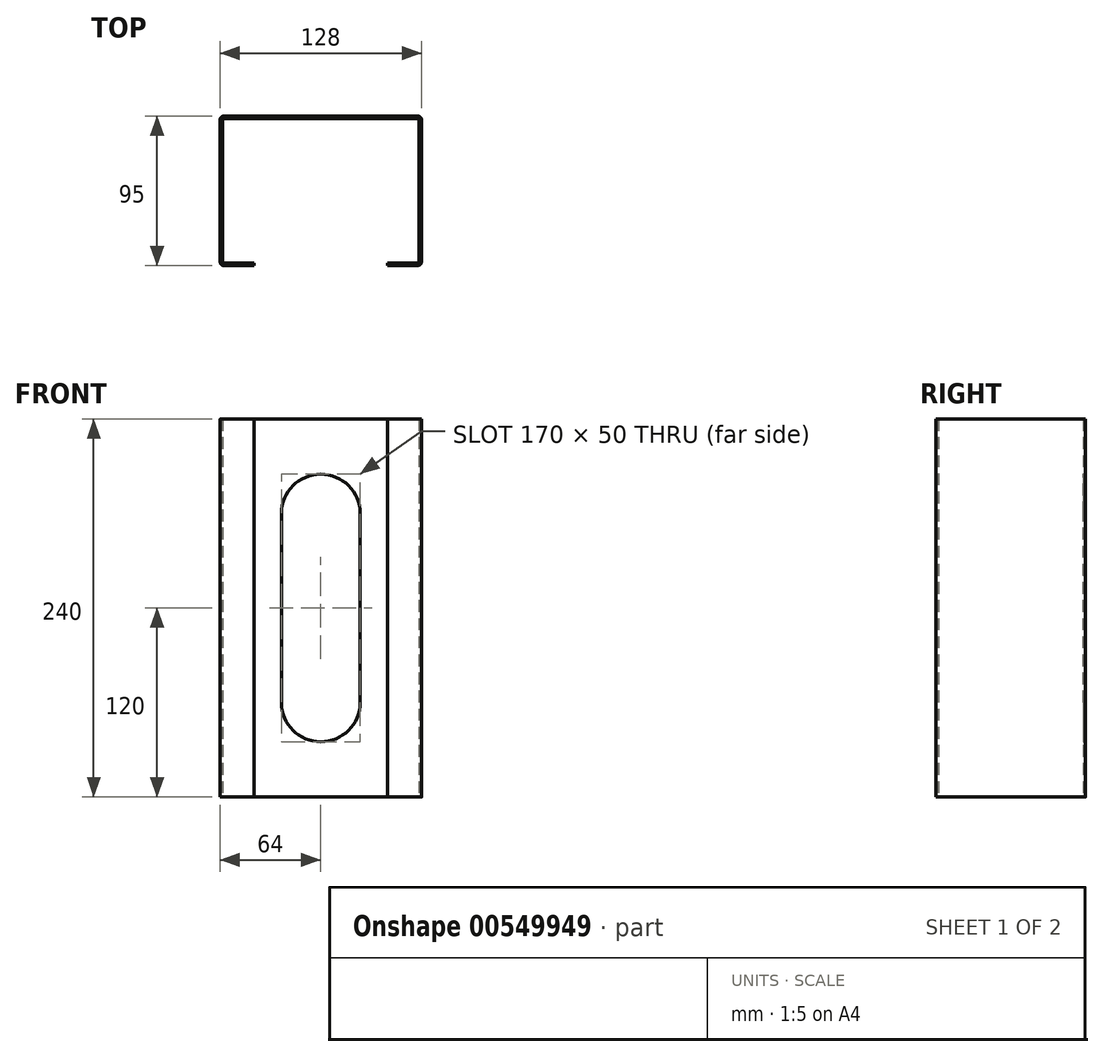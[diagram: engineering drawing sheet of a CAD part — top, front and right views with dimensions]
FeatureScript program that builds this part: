
annotation { "Feature Type Name" : "Feature", "Feature Type Description" : "" }
export const myFeature = defineFeature(function(context is Context, id is Id, definition is map)
    precondition{}
    {
        {
            var Q0;
            Q0=qCreatedBy(makeId("Top.planeOp"),FACE);
            var sketch = newSketch(context, id + "F0", { "sketchPlane" : qUnion([Q0])});
            skLineSegment(sketch, "E0.bottom", {"start": v(-61.5, 46) * mm, "end": v(61.5, 46) * mm});
            skLineSegment(sketch, "E0.top", {"start": v(-61.5, -46) * mm, "end": v(-42.5, -46) * mm});
            skLineSegment(sketch, "E0.left", {"start": v(-62.5, 45) * mm, "end": v(-62.5, -45) * mm});
            skLineSegment(sketch, "E0.right", {"start": v(62.5, 45) * mm, "end": v(62.5, -45) * mm});
            skPoint(sketch, "E0.middle", {"position": v(0, 0) * mm});
            skLineSegment(sketch, "E1.bottom", {"start": v(61.5, -47.5) * mm, "end": v(42.5, -47.5) * mm});
            skLineSegment(sketch, "E1.top", {"start": v(61.5, 47.5) * mm, "end": v(-61.5, 47.5) * mm});
            skLineSegment(sketch, "E1.left", {"start": v(64, -45) * mm, "end": v(64, 45) * mm});
            skLineSegment(sketch, "E1.right", {"start": v(-64, -45) * mm, "end": v(-64, 45) * mm});
            skPoint(sketch, "E2.middle", {"position": v(0, -47.5) * mm});
            skLineSegment(sketch, "E3.left", {"start": v(42.5, -47.5) * mm, "end": v(42.5, -46) * mm});
            skLineSegment(sketch, "E3.right", {"start": v(-42.5, -47.5) * mm, "end": v(-42.5, -46) * mm});
            skLineSegment(sketch, "E4.trimOffspring", {"start": v(42.5, -46) * mm, "end": v(61.5, -46) * mm});
            skLineSegment(sketch, "E5.trimOffspring", {"start": v(-42.5, -47.5) * mm, "end": v(-61.5, -47.5) * mm});
            skPoint(sketch, "E6.visualSharp", {"position": v(-62.5, -46) * mm});
            skArc(sketch, "E6.filletArc", {"start": v(-62.5, -45) * mm, "mid": v(-62.2, -45.7) * mm, "end": v(-61.5, -46) * mm});
            skPoint(sketch, "E7.visualSharp", {"position": v(-64, -47.5) * mm});
            skArc(sketch, "E7.filletArc", {"start": v(-64, -45) * mm, "mid": v(-63.27, -46.77) * mm, "end": v(-61.5, -47.5) * mm});
            skPoint(sketch, "E8.visualSharp", {"position": v(-64, 47.5) * mm});
            skArc(sketch, "E8.filletArc", {"start": v(-61.5, 47.5) * mm, "mid": v(-63.27, 46.77) * mm, "end": v(-64, 45) * mm});
            skPoint(sketch, "E9.visualSharp", {"position": v(64, -47.5) * mm});
            skArc(sketch, "E9.filletArc", {"start": v(61.5, -47.5) * mm, "mid": v(63.27, -46.77) * mm, "end": v(64, -45) * mm});
            skPoint(sketch, "E10.visualSharp", {"position": v(64, 47.5) * mm});
            skArc(sketch, "E10.filletArc", {"start": v(64, 45) * mm, "mid": v(63.27, 46.77) * mm, "end": v(61.5, 47.5) * mm});
            skPoint(sketch, "E11.visualSharp", {"position": v(62.5, 46) * mm});
            skArc(sketch, "E11.filletArc", {"start": v(62.5, 45) * mm, "mid": v(62.2, 45.7) * mm, "end": v(61.5, 46) * mm});
            skPoint(sketch, "E12.visualSharp", {"position": v(62.5, -46) * mm});
            skArc(sketch, "E12.filletArc", {"start": v(61.5, -46) * mm, "mid": v(62.2, -45.7) * mm, "end": v(62.5, -45) * mm});
            skPoint(sketch, "E13.visualSharp", {"position": v(-62.5, 46) * mm});
            skArc(sketch, "E13.filletArc", {"start": v(-61.5, 46) * mm, "mid": v(-62.2, 45.7) * mm, "end": v(-62.5, 45) * mm});
            skSolve(sketch);
        }
        {
            var Q0;
            Q0=makeQuery(id+"F0.imprint","IMPRINT",FACE,{"disambiguationData":[TD([[makeQuery(id+"F0.imprint","IMPRINT",EDGE,{"derivedFrom":sQuery(id+"F0.wireOp",EDGE,"E0.bottom")}),1.0]])]});
            extrude(context, id + "F1", {"entities" : qUnion([Q0]), "endBound" : BoundingType.SYMMETRIC, "depth" : 240 * mm, "offsetDistance" : 25 * mm});
        }
        {
            var Q0;
            Q0=makeQuery(id+"F1.opExtrude","SWEPT_FACE",FACE,{"disambiguationData":[OSD([sQuery(id+"F0.wireOp",EDGE,"E1.top")])]});
            var sketch = newSketch(context, id + "F2", { "sketchPlane" : qUnion([Q0])});
            skSolve(sketch);
        }
        {
            var Q0;
            {var subQ0=sQuery(id+"F0.wireOp",EDGE,"E1.top");Q0=makeQuery(id+"F2.imprint","IMPRINT",FACE,{"disambiguationData":[TD([[makeQuery(id+"F2.imprint","IMPRINT",EDGE,{"derivedFrom":makeQuery(id+"F1.opExtrude","CAP_EDGE",EDGE,{"disambiguationData":[OSD([subQ0])],"isStart":true})}),1.0]])]});}
            var sketch = newSketch(context, id + "F3", { "sketchPlane" : qUnion([Q0])});
            skArc(sketch, "E14", {"start": v(-25, -60) * mm, "mid": v(0, -85) * mm, "end": v(25, -60) * mm});
            skArc(sketch, "E15", {"start": v(25, 60) * mm, "mid": v(0, 85) * mm, "end": v(-25, 60) * mm});
            skLineSegment(sketch, "E16", {"start": v(-25, -60) * mm, "end": v(-25, 60) * mm});
            skLineSegment(sketch, "E17", {"start": v(25, 60) * mm, "end": v(25, -60) * mm});
            skLineSegment(sketch, "E18", {"start": v(-64.45, 0) * mm, "end": v(65.2, 0) * mm, "construction": true});
            skSolve(sketch);
        }
        {
            var Q0;
            Q0=makeQuery(id+"F3.imprint","IMPRINT",FACE,{"disambiguationData":[TD([[makeQuery(id+"F3.imprint","IMPRINT",EDGE,{"derivedFrom":sQuery(id+"F3.wireOp",EDGE,"E14")}),1.0]])]});
            extrude(context, id + "F4", {"entities" : qUnion([Q0]), "operationType" : NewBodyOperationType.REMOVE, "oppositeDirection" : true, "depth" : 25 * mm, "offsetDistance" : 25 * mm});
        }
    });
